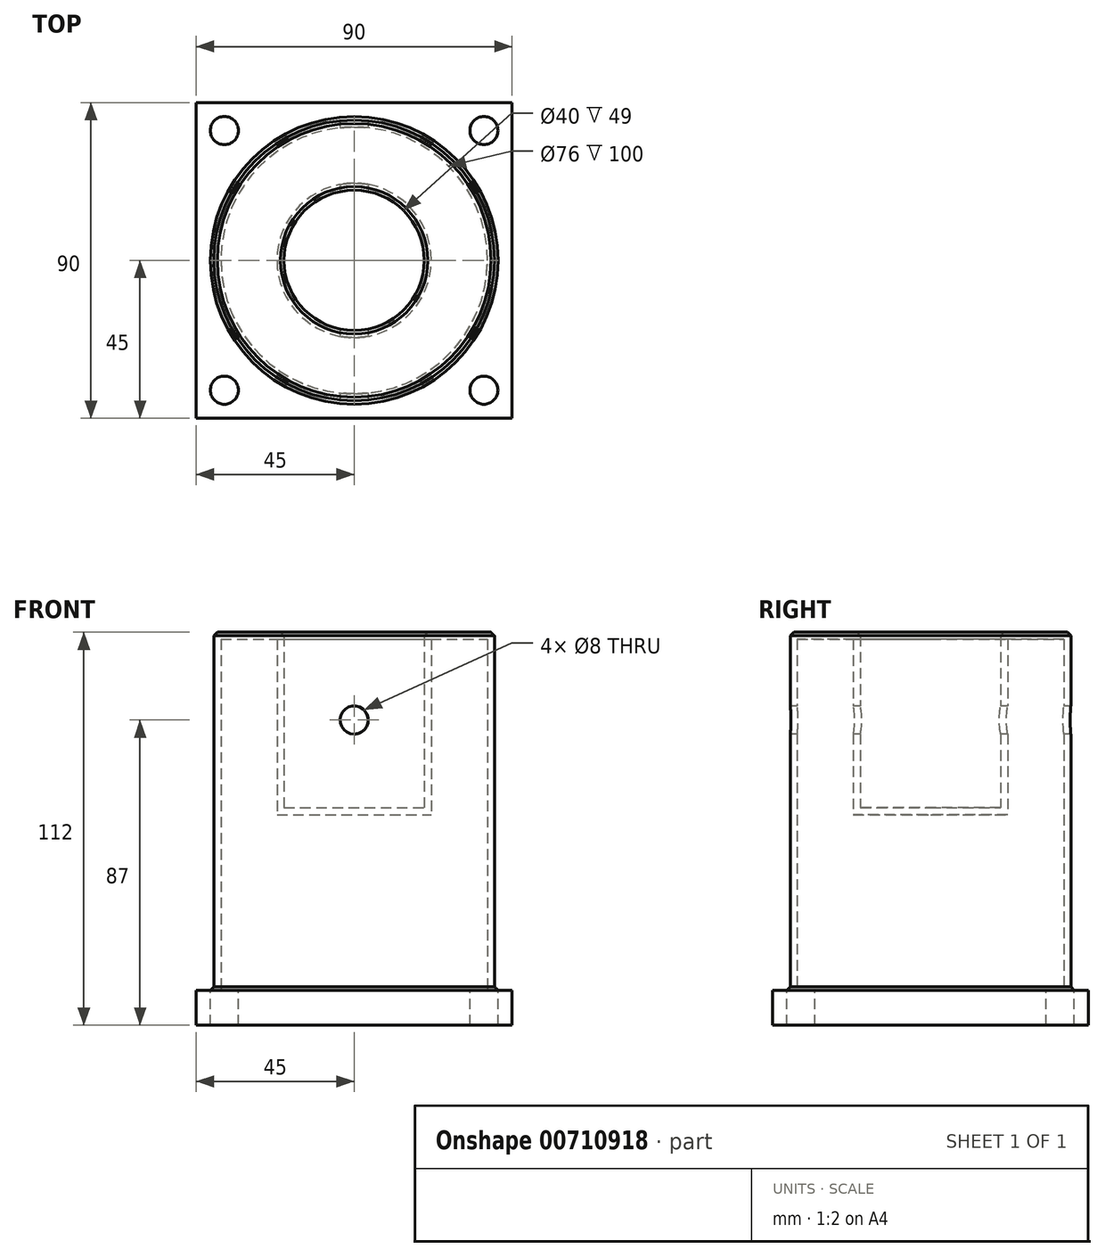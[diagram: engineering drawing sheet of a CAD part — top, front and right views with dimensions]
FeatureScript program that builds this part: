
annotation { "Feature Type Name" : "Feature", "Feature Type Description" : "" }
export const myFeature = defineFeature(function(context is Context, id is Id, definition is map)
    precondition{}
    {
        {
            var Q0;
            Q0=qCreatedBy(makeId("Top.planeOp"),FACE);
            var sketch = newSketch(context, id + "F0", { "sketchPlane" : qUnion([Q0])});
            skLineSegment(sketch, "E0.bottom", {"start": v(45, 45) * mm, "end": v(-45, 45) * mm});
            skLineSegment(sketch, "E0.top", {"start": v(45, -45) * mm, "end": v(-45, -45) * mm});
            skLineSegment(sketch, "E0.left", {"start": v(45, 45) * mm, "end": v(45, -45) * mm});
            skLineSegment(sketch, "E0.right", {"start": v(-45, 45) * mm, "end": v(-45, -45) * mm});
            skPoint(sketch, "E0.middle", {"position": v(0, 0) * mm});
            skCircle(sketch, "E1", {"center": v(-37, 37) * mm, "radius": 4 * mm});
            skCircle(sketch, "E2.MirrorC", {"center": v(37, 37) * mm, "radius": 4 * mm});
            skCircle(sketch, "E3.MirrorC", {"center": v(-37, -37) * mm, "radius": 4 * mm});
            skCircle(sketch, "E4.MirrorC", {"center": v(37, -37) * mm, "radius": 4 * mm});
            skSolve(sketch);
        }
        {
            var Q0;
            Q0=makeQuery(id+"F0.imprint","IMPRINT",FACE,{"disambiguationData":[TD([[makeQuery(id+"F0.imprint","IMPRINT",EDGE,{"derivedFrom":sQuery(id+"F0.wireOp",EDGE,"E0.bottom")}),1.0]])]});
            extrude(context, id + "F1", {"entities" : qUnion([Q0]), "oppositeDirection" : true, "depth" : 10 * mm, "offsetDistance" : 25 * mm});
        }
        {
            var Q0;
            Q0=makeQuery(id+"F1.opExtrude","CAP_FACE",FACE,{"disambiguationData":[OSD([sQuery(id+"F0.wireOp",EDGE,"E0.bottom"),sQuery(id+"F0.wireOp",EDGE,"E0.top"),sQuery(id+"F0.wireOp",EDGE,"E0.left"),sQuery(id+"F0.wireOp",EDGE,"E0.right"),sQuery(id+"F0.wireOp",EDGE,"E1"),sQuery(id+"F0.wireOp",EDGE,"E2.MirrorC"),sQuery(id+"F0.wireOp",EDGE,"E3.MirrorC"),sQuery(id+"F0.wireOp",EDGE,"E4.MirrorC")])],"isStart":true});
            var sketch = newSketch(context, id + "F2", { "sketchPlane" : qUnion([Q0])});
            skCircle(sketch, "E5", {"center": v(0, 0) * mm, "radius": 40 * mm});
            skCircle(sketch, "E6.0", {"center": v(0, 0) * mm, "radius": 38 * mm});
            skSolve(sketch);
        }
        {
            var Q0;
            Q0=makeQuery(id+"F2.imprint","IMPRINT",FACE,{"disambiguationData":[TD([[makeQuery(id+"F2.imprint","IMPRINT",EDGE,{"derivedFrom":sQuery(id+"F2.wireOp",EDGE,"E5")}),1.0]])]});
            extrude(context, id + "F3", {"entities" : qUnion([Q0]), "operationType" : NewBodyOperationType.ADD, "depth" : 100 * mm, "offsetDistance" : 25 * mm});
        }
        {
            var Q0;
            Q0=makeQuery(id+"F3.opExtrude","CAP_FACE",FACE,{"disambiguationData":[OSD([sQuery(id+"F2.wireOp",EDGE,"E5"),sQuery(id+"F2.wireOp",EDGE,"E6.0")])],"isStart":false});
            var sketch = newSketch(context, id + "F4", { "sketchPlane" : qUnion([Q0])});
            skCircle(sketch, "E7", {"center": v(0, 0) * mm, "radius": 39.92 * mm});
            skSolve(sketch);
        }
        {
            var Q0;
            Q0=qCreatedBy(makeId("Front.planeOp"),FACE);
            var sketch = newSketch(context, id + "F5", { "sketchPlane" : qUnion([Q0])});
            skLineSegment(sketch, "E8", {"start": v(0, 50) * mm, "end": v(22, 50) * mm});
            skLineSegment(sketch, "E9", {"start": v(22, 50) * mm, "end": v(22, 100) * mm});
            skLineSegment(sketch, "E10", {"start": v(22, 100) * mm, "end": v(40, 100) * mm});
            skLineSegment(sketch, "E11", {"start": v(40, 100) * mm, "end": v(40, 102) * mm});
            skLineSegment(sketch, "E12", {"start": v(40, 102) * mm, "end": v(20, 102) * mm});
            skLineSegment(sketch, "E13", {"start": v(20, 102) * mm, "end": v(20, 52) * mm});
            skLineSegment(sketch, "E14", {"start": v(20, 52) * mm, "end": v(0, 52) * mm});
            skLineSegment(sketch, "E15", {"start": v(0, 52) * mm, "end": v(0, 50) * mm});
            skLineSegment(sketch, "E16", {"start": v(0, 50) * mm, "end": v(0, 100.3) * mm, "construction": true});
            skSolve(sketch);
        }
        {
            var Q0;
            Q0=makeQuery(id+"F5.imprint","IMPRINT",FACE,{"disambiguationData":[TD([[makeQuery(id+"F5.imprint","IMPRINT",EDGE,{"derivedFrom":sQuery(id+"F5.wireOp",EDGE,"E8")}),1.0]])]});
            var Q1;
            Q1=sQuery(id+"F5.wireOp",EDGE,"E16");
            revolve(context, id + "F6", {"operationType" : NewBodyOperationType.ADD, "entities" : qUnion([Q0]), "axis" : qUnion([Q1]), "revolveType" : RevolveType.FULL});
        }
        {
            var Q0;
            Q0=makeQuery(id+"F6.boolean.opBoolean","MERGE",FACE,{"derivedFrom":[makeQuery(id+"F3.opExtrude","SWEPT_FACE",FACE,{"disambiguationData":[OSD([sQuery(id+"F2.wireOp",EDGE,"E5")])]}),makeQuery(id+"F6.opRevolve","SWEPT_FACE",FACE,{"disambiguationData":[OSD([sQuery(id+"F5.wireOp",EDGE,"E11")])]})]});
            chamfer(context, id + "F7", {"entities" : qUnion([Q0]), "width" : 1 * mm, "tangentPropagation" : true});
        }
        {
            var Q0;
            Q0=makeQuery(id+"F6.opRevolve","SWEPT_EDGE",EDGE,{"disambiguationData":[OSD([sQuery(id+"F5.wireOp",EDGE,"E12"),sQuery(id+"F5.wireOp",EDGE,"E13")])]});
            chamfer(context, id + "F8", {"entities" : qUnion([Q0]), "width" : 1 * mm, "tangentPropagation" : true});
        }
        {
            var Q0;
            Q0=qCreatedBy(makeId("Front.planeOp"),FACE);
            cPlane(context, id + "F9", {"entities" : qUnion([Q0]), "cplaneType" : CPlaneType.OFFSET, "offset" : 40 * mm, "width" : 150 * mm, "height" : 150 * mm});
        }
        {
            var Q0;
            Q0=qCreatedBy(id+"F9.planeOp",FACE);
            var sketch = newSketch(context, id + "F10", { "sketchPlane" : qUnion([Q0])});
            skCircle(sketch, "E17", {"center": v(0, 77) * mm, "radius": 4 * mm});
            skSolve(sketch);
        }
        {
            var Q0;
            Q0=makeQuery(id+"F10.imprint","IMPRINT",FACE,{"disambiguationData":[TD([[makeQuery(id+"F10.imprint","IMPRINT",EDGE,{"derivedFrom":sQuery(id+"F10.wireOp",EDGE,"E17")}),1.0]])]});
            extrude(context, id + "F11", {"entities" : qUnion([Q0]), "operationType" : NewBodyOperationType.REMOVE, "oppositeDirection" : true, "depth" : 80 * mm, "offsetDistance" : 25 * mm});
        }
    });
